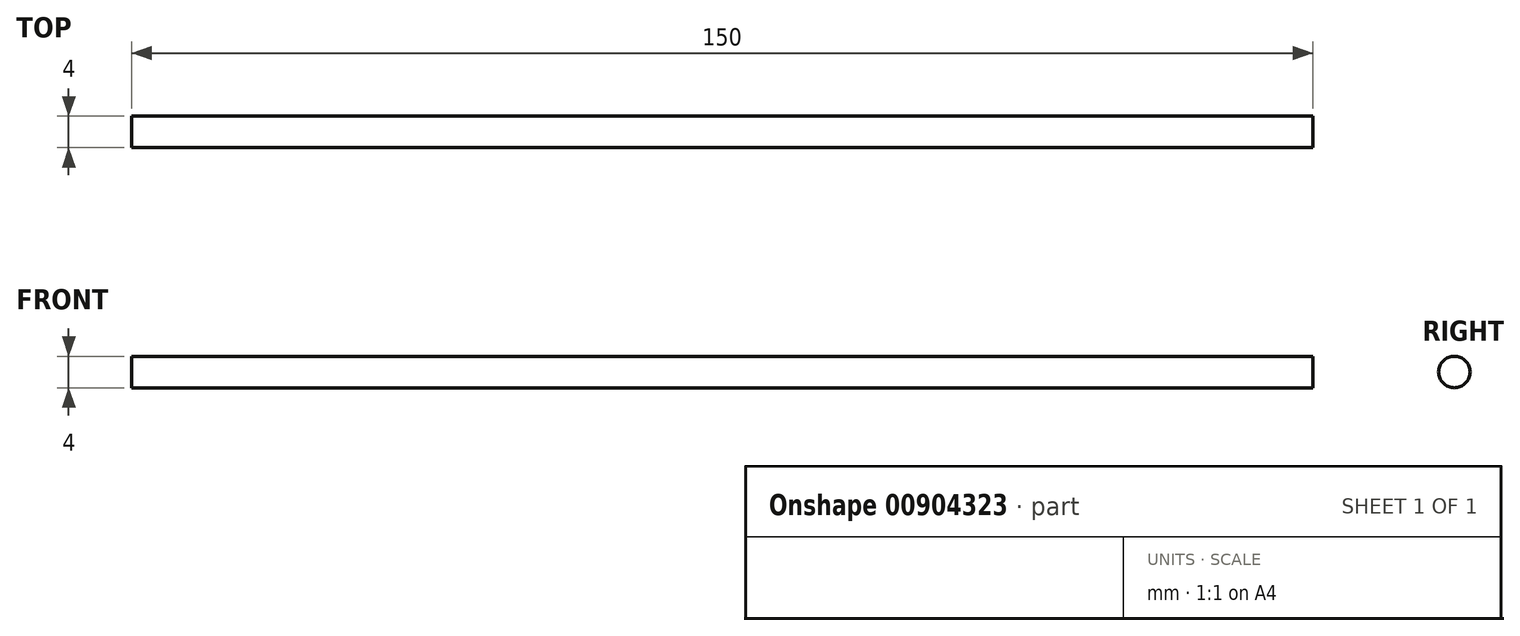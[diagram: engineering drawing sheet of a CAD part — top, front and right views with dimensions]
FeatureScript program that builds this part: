
annotation { "Feature Type Name" : "Feature", "Feature Type Description" : "" }
export const myFeature = defineFeature(function(context is Context, id is Id, definition is map)
    precondition{}
    {
        {
            var Q0;
            Q0=qCreatedBy(makeId("Front.planeOp"),FACE);
            var sketch = newSketch(context, id + "F0", { "sketchPlane" : qUnion([Q0])});
            skLineSegment(sketch, "E0.bottom", {"start": v(0, 0) * mm, "end": v(-150, 0) * mm});
            skLineSegment(sketch, "E0.top", {"start": v(0, 2) * mm, "end": v(-150, 2) * mm});
            skLineSegment(sketch, "E0.left", {"start": v(0, 0) * mm, "end": v(0, 2) * mm});
            skLineSegment(sketch, "E0.right", {"start": v(-150, 0) * mm, "end": v(-150, 2) * mm});
            skSolve(sketch);
        }
        {
            var Q0;
            Q0=makeQuery(id+"F0.imprint","IMPRINT",FACE,{"disambiguationData":[TD([[makeQuery(id+"F0.imprint","IMPRINT",EDGE,{"derivedFrom":sQuery(id+"F0.wireOp",EDGE,"E0.bottom")}),-1.0]])]});
            var Q1;
            Q1=sQuery(id+"F0.wireOp",EDGE,"E0.bottom");
            revolve(context, id + "F1", {"surfaceOperationType" : NewSurfaceOperationType.NEW, "entities" : qUnion([Q0]), "axis" : qUnion([Q1]), "revolveType" : RevolveType.FULL});
        }
    });
